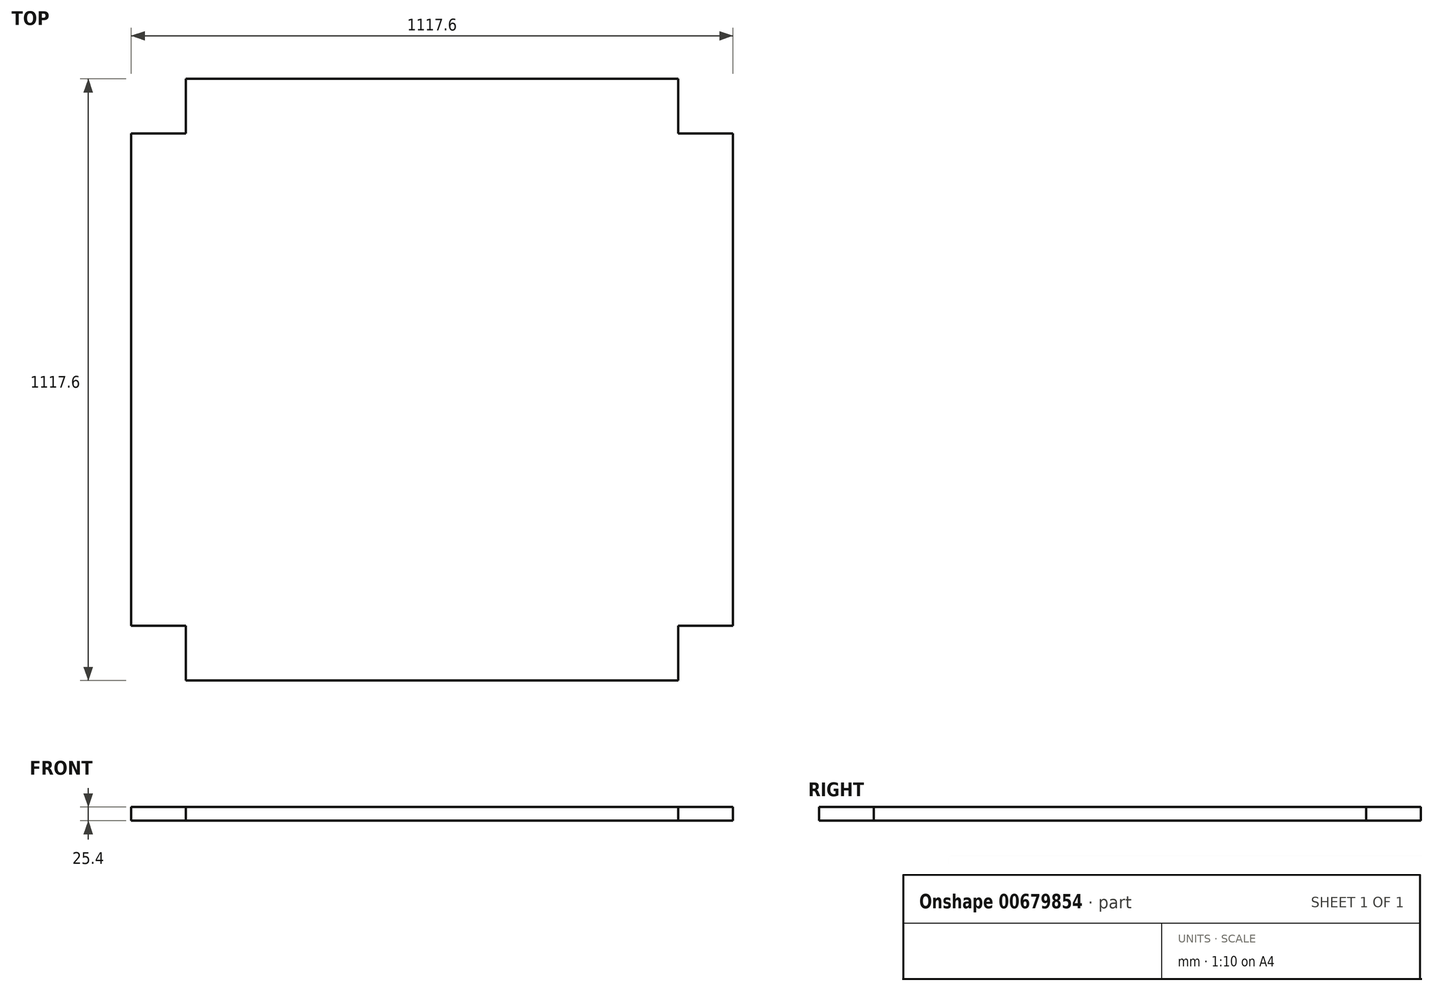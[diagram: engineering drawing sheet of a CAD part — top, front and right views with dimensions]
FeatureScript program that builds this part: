
annotation { "Feature Type Name" : "Feature", "Feature Type Description" : "" }
export const myFeature = defineFeature(function(context is Context, id is Id, definition is map)
    precondition{}
    {
        {
            var Q0;
            Q0=qCreatedBy(makeId("Top.planeOp"),FACE);
            var sketch = newSketch(context, id + "F0", { "sketchPlane" : qUnion([Q0])});
            skLineSegment(sketch, "E0.bottom", {"start": v(-107.65, 1027.37) * mm, "end": v(1009.95, 1027.37) * mm});
            skLineSegment(sketch, "E0.top", {"start": v(-107.65, -90.23) * mm, "end": v(1009.95, -90.23) * mm});
            skLineSegment(sketch, "E0.left", {"start": v(-107.65, 1027.37) * mm, "end": v(-107.65, -90.23) * mm});
            skLineSegment(sketch, "E0.right", {"start": v(1009.95, 1027.37) * mm, "end": v(1009.95, -90.23) * mm});
            skSolve(sketch);
        }
        {
            var Q0;
            Q0=makeQuery(id+"F0.imprint","IMPRINT",FACE,{"disambiguationData":[TD([[makeQuery(id+"F0.imprint","IMPRINT",EDGE,{"derivedFrom":sQuery(id+"F0.wireOp",EDGE,"E0.bottom")}),-1.0]])]});
            extrude(context, id + "F1", {"entities" : qUnion([Q0]), "depth" : 25.4 * mm, "offsetDistance" : 25.4 * mm});
        }
        {
            var Q0;
            Q0=makeQuery(id+"F1.opExtrude","CAP_FACE",FACE,{"disambiguationData":[OSD([sQuery(id+"F0.wireOp",EDGE,"E0.bottom"),sQuery(id+"F0.wireOp",EDGE,"E0.top"),sQuery(id+"F0.wireOp",EDGE,"E0.left"),sQuery(id+"F0.wireOp",EDGE,"E0.right")])],"isStart":false});
            var sketch = newSketch(context, id + "F2", { "sketchPlane" : qUnion([Q0])});
            skLineSegment(sketch, "E1.bottom", {"start": v(-107.65, 1027.37) * mm, "end": v(-6.05, 1027.37) * mm});
            skLineSegment(sketch, "E1.top", {"start": v(-107.65, 925.77) * mm, "end": v(-6.05, 925.77) * mm});
            skLineSegment(sketch, "E1.left", {"start": v(-107.65, 1027.37) * mm, "end": v(-107.65, 925.77) * mm});
            skLineSegment(sketch, "E1.right", {"start": v(-6.05, 1027.37) * mm, "end": v(-6.05, 925.77) * mm});
            skLineSegment(sketch, "E2.bottom", {"start": v(1009.95, 1027.37) * mm, "end": v(908.35, 1027.37) * mm});
            skLineSegment(sketch, "E2.top", {"start": v(1009.95, 925.77) * mm, "end": v(908.35, 925.77) * mm});
            skLineSegment(sketch, "E2.left", {"start": v(1009.95, 1027.37) * mm, "end": v(1009.95, 925.77) * mm});
            skLineSegment(sketch, "E2.right", {"start": v(908.35, 1027.37) * mm, "end": v(908.35, 925.77) * mm});
            skLineSegment(sketch, "E3.bottom", {"start": v(-107.65, -90.23) * mm, "end": v(-6.05, -90.23) * mm});
            skLineSegment(sketch, "E3.top", {"start": v(-107.65, 11.37) * mm, "end": v(-6.05, 11.37) * mm});
            skLineSegment(sketch, "E3.left", {"start": v(-107.65, -90.23) * mm, "end": v(-107.65, 11.37) * mm});
            skLineSegment(sketch, "E3.right", {"start": v(-6.05, -90.23) * mm, "end": v(-6.05, 11.37) * mm});
            skLineSegment(sketch, "E4.bottom", {"start": v(1009.95, -90.23) * mm, "end": v(908.35, -90.23) * mm});
            skLineSegment(sketch, "E4.top", {"start": v(1009.95, 11.37) * mm, "end": v(908.35, 11.37) * mm});
            skLineSegment(sketch, "E4.left", {"start": v(1009.95, -90.23) * mm, "end": v(1009.95, 11.37) * mm});
            skLineSegment(sketch, "E4.right", {"start": v(908.35, -90.23) * mm, "end": v(908.35, 11.37) * mm});
            skSolve(sketch);
        }
        {
            var Q0;
            Q0=makeQuery(id+"F2.imprint","IMPRINT",FACE,{"disambiguationData":[TD([[makeQuery(id+"F2.imprint","IMPRINT",EDGE,{"derivedFrom":sQuery(id+"F2.wireOp",EDGE,"E3.bottom")}),1.0]])]});
            var Q1;
            Q1=makeQuery(id+"F2.imprint","IMPRINT",FACE,{"disambiguationData":[TD([[makeQuery(id+"F2.imprint","IMPRINT",EDGE,{"derivedFrom":sQuery(id+"F2.wireOp",EDGE,"E4.bottom")}),1.0]])]});
            var Q2;
            Q2=makeQuery(id+"F2.imprint","IMPRINT",FACE,{"disambiguationData":[TD([[makeQuery(id+"F2.imprint","IMPRINT",EDGE,{"derivedFrom":sQuery(id+"F2.wireOp",EDGE,"E2.bottom")}),-1.0]])]});
            var Q3;
            Q3=makeQuery(id+"F2.imprint","IMPRINT",FACE,{"disambiguationData":[TD([[makeQuery(id+"F2.imprint","IMPRINT",EDGE,{"derivedFrom":sQuery(id+"F2.wireOp",EDGE,"E1.bottom")}),-1.0]])]});
            extrude(context, id + "F3", {"entities" : qUnion([Q0, Q1, Q2, Q3]), "operationType" : NewBodyOperationType.REMOVE, "oppositeDirection" : true, "depth" : 25.4 * mm, "offsetDistance" : 25.4 * mm});
        }
    });
